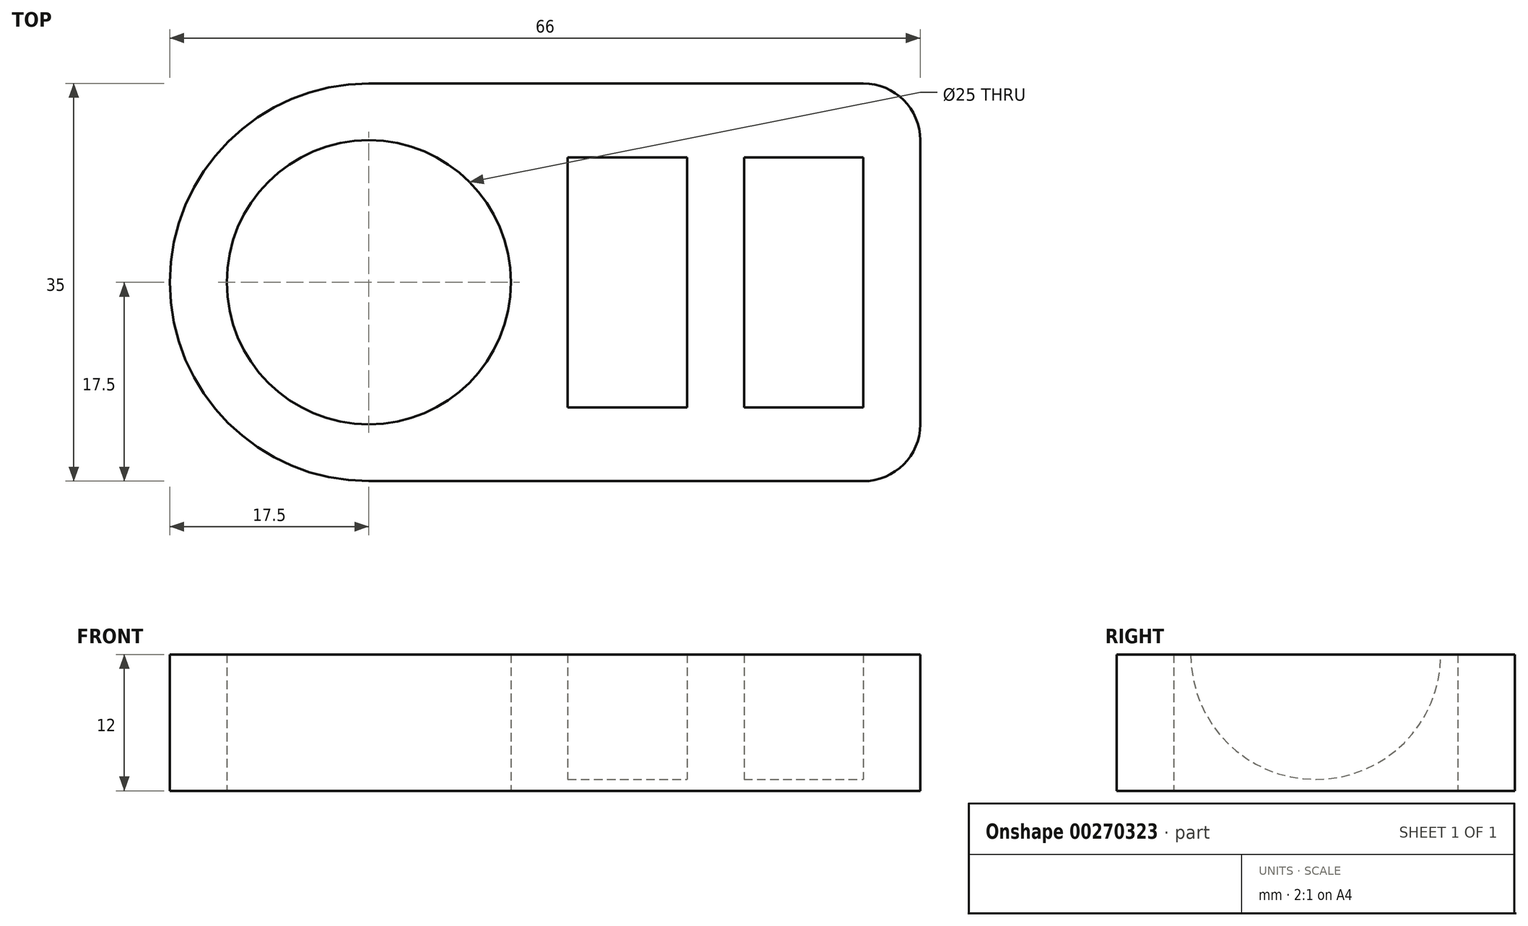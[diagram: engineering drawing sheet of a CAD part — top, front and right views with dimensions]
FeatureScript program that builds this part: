
annotation { "Feature Type Name" : "Feature", "Feature Type Description" : "" }
export const myFeature = defineFeature(function(context is Context, id is Id, definition is map)
    precondition{}
    {
        {
            var Q0;
            Q0=qCreatedBy(makeId("Top.planeOp"),FACE);
            var sketch = newSketch(context, id + "F0", { "sketchPlane" : qUnion([Q0])});
            skLineSegment(sketch, "E0.bottom", {"start": v(17.5, 0) * mm, "end": v(61, 0) * mm});
            skLineSegment(sketch, "E0.top", {"start": v(17.5, 35) * mm, "end": v(61, 35) * mm});
            skLineSegment(sketch, "E0.left", {"start": v(0, 17.5) * mm, "end": v(0, 17.5) * mm});
            skLineSegment(sketch, "E0.right", {"start": v(66, 5) * mm, "end": v(66, 30) * mm});
            skLineSegment(sketch, "E1.bottom", {"start": v(0, 0) * mm, "end": v(17.5, 0) * mm, "construction": true});
            skLineSegment(sketch, "E1.top", {"start": v(0, 17.5) * mm, "end": v(17.5, 17.5) * mm, "construction": true});
            skLineSegment(sketch, "E1.left", {"start": v(0, 0) * mm, "end": v(0, 17.5) * mm, "construction": true});
            skLineSegment(sketch, "E1.right", {"start": v(17.5, 0) * mm, "end": v(17.5, 17.5) * mm, "construction": true});
            skCircle(sketch, "E2", {"center": v(17.5, 17.5) * mm, "radius": 12.5 * mm});
            skPoint(sketch, "E3.visualSharp", {"position": v(0, 0) * mm});
            skArc(sketch, "E3.filletArc", {"start": v(0, 17.5) * mm, "mid": v(5.13, 5.13) * mm, "end": v(17.5, 0) * mm});
            skPoint(sketch, "E4.visualSharp", {"position": v(0, 35) * mm});
            skArc(sketch, "E4.filletArc", {"start": v(17.5, 35) * mm, "mid": v(5.13, 29.87) * mm, "end": v(0, 17.5) * mm});
            skPoint(sketch, "E5.visualSharp", {"position": v(66, 35) * mm});
            skArc(sketch, "E5.filletArc", {"start": v(66, 30) * mm, "mid": v(64.54, 33.54) * mm, "end": v(61, 35) * mm});
            skPoint(sketch, "E6.visualSharp", {"position": v(66, 0) * mm});
            skArc(sketch, "E6.filletArc", {"start": v(61, 0) * mm, "mid": v(64.54, 1.46) * mm, "end": v(66, 5) * mm});
            skSolve(sketch);
        }
        {
            var Q0;
            Q0=makeQuery(id+"F0.imprint","IMPRINT",FACE,{"disambiguationData":[TD([[makeQuery(id+"F0.imprint","IMPRINT",EDGE,{"derivedFrom":sQuery(id+"F0.wireOp",EDGE,"E0.bottom")}),1.0]])]});
            extrude(context, id + "F1", {"entities" : qUnion([Q0]), "depth" : 12 * mm});
        }
        {
            var Q0;
            Q0=makeQuery(id+"F1.opExtrude","CAP_FACE",FACE,{"disambiguationData":[OSD([sQuery(id+"F0.wireOp",EDGE,"E0.bottom"),sQuery(id+"F0.wireOp",EDGE,"E0.top"),sQuery(id+"F0.wireOp",EDGE,"E0.right"),sQuery(id+"F0.wireOp",EDGE,"E2"),sQuery(id+"F0.wireOp",EDGE,"E3.filletArc"),sQuery(id+"F0.wireOp",EDGE,"E4.filletArc"),sQuery(id+"F0.wireOp",EDGE,"E5.filletArc"),sQuery(id+"F0.wireOp",EDGE,"E6.filletArc")])],"isStart":false});
            var sketch = newSketch(context, id + "F2", { "sketchPlane" : qUnion([Q0])});
            skLineSegment(sketch, "E7.bottom", {"start": v(0, 0) * mm, "end": v(35, 0) * mm, "construction": true});
            skLineSegment(sketch, "E7.top", {"start": v(0, 17.5) * mm, "end": v(35, 17.5) * mm, "construction": true});
            skLineSegment(sketch, "E7.left", {"start": v(0, 0) * mm, "end": v(0, 17.5) * mm, "construction": true});
            skLineSegment(sketch, "E7.right", {"start": v(35, 0) * mm, "end": v(35, 17.5) * mm, "construction": true});
            skLineSegment(sketch, "E8.bottom", {"start": v(35, 17.5) * mm, "end": v(45.5, 17.5) * mm});
            skLineSegment(sketch, "E8.top", {"start": v(35, 6.5) * mm, "end": v(45.5, 6.5) * mm});
            skLineSegment(sketch, "E8.left", {"start": v(35, 17.5) * mm, "end": v(35, 6.5) * mm});
            skLineSegment(sketch, "E8.right", {"start": v(45.5, 17.5) * mm, "end": v(45.5, 6.5) * mm});
            skLineSegment(sketch, "E9", {"start": v(45.5, 17.5) * mm, "end": v(50.5, 17.5) * mm, "construction": true});
            skLineSegment(sketch, "E10.bottom", {"start": v(50.5, 17.5) * mm, "end": v(61, 17.5) * mm});
            skLineSegment(sketch, "E10.top", {"start": v(50.5, 6.5) * mm, "end": v(61, 6.5) * mm});
            skLineSegment(sketch, "E10.left", {"start": v(50.5, 17.5) * mm, "end": v(50.5, 6.5) * mm});
            skLineSegment(sketch, "E10.right", {"start": v(61, 17.5) * mm, "end": v(61, 6.5) * mm});
            skSolve(sketch);
        }
        {
            var Q0;
            Q0 = qSketchRegion(id + "F2", true);
            var Q1;
            Q1=sQuery(id+"F2.wireOp",EDGE,"E8.bottom");
            revolve(context, id + "F3", {"operationType" : NewBodyOperationType.REMOVE, "entities" : qUnion([Q0]), "axis" : qUnion([Q1]), "revolveType" : RevolveType.FULL, "oppositeDirection" : true});
        }
    });
